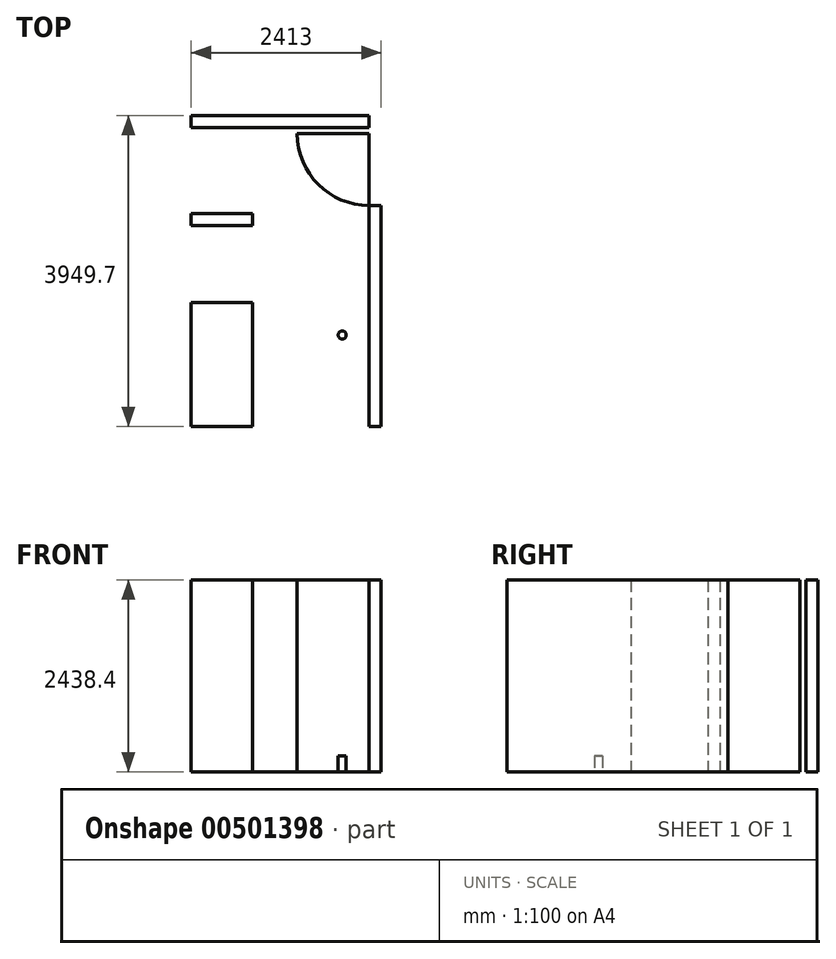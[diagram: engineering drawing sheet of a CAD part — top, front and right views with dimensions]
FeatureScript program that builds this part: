
annotation { "Feature Type Name" : "Feature", "Feature Type Description" : "" }
export const myFeature = defineFeature(function(context is Context, id is Id, definition is map)
    precondition{}
    {
        {
            var Q0;
            Q0=qCreatedBy(makeId("Top.planeOp"),FACE);
            var sketch = newSketch(context, id + "F0", { "sketchPlane" : qUnion([Q0])});
            skLineSegment(sketch, "E0.bottom", {"start": v(0, 0) * mm, "end": v(2260.6, 0) * mm});
            skLineSegment(sketch, "E0.top", {"start": v(0, 2705.1) * mm, "end": v(781.05, 2705.1) * mm});
            skLineSegment(sketch, "E0.left", {"start": v(0, 0) * mm, "end": v(0, 2705.1) * mm});
            skLineSegment(sketch, "E1", {"start": v(0, 2705.1) * mm, "end": v(0, 3797.3) * mm});
            skLineSegment(sketch, "E2", {"start": v(0, 3797.3) * mm, "end": v(2260.6, 3797.3) * mm});
            skLineSegment(sketch, "E3", {"start": v(2260.6, 3797.3) * mm, "end": v(2260.6, 0) * mm});
            skLineSegment(sketch, "E4", {"start": v(2260.6, 3797.3) * mm, "end": v(2260.6, 3721.1) * mm, "construction": true});
            skArc(sketch, "E5", {"start": v(1346.2, 3721.1) * mm, "mid": v(1614.02, 3074.52) * mm, "end": v(2260.6, 2806.7) * mm});
            skLineSegment(sketch, "E6", {"start": v(1346.2, 3721.1) * mm, "end": v(2260.6, 3721.1) * mm});
            skLineSegment(sketch, "E7", {"start": v(0, 3797.3) * mm, "end": v(0, 3721.1) * mm, "construction": true});
            skLineSegment(sketch, "E8", {"start": v(0, 3721.1) * mm, "end": v(0, 2806.7) * mm, "construction": true});
            skCircle(sketch, "E9", {"center": v(1917.7, 1162.05) * mm, "radius": 50.8 * mm});
            skLineSegment(sketch, "E10", {"start": v(781.05, 2705.1) * mm, "end": v(781.05, 2552.7) * mm});
            skLineSegment(sketch, "E11", {"start": v(781.05, 2552.7) * mm, "end": v(0, 2552.7) * mm});
            skLineSegment(sketch, "E12", {"start": v(781.05, 1574.8) * mm, "end": v(0, 1574.8) * mm});
            skLineSegment(sketch, "E13.trimOffspring", {"start": v(781.05, 1574.8) * mm, "end": v(781.05, 0) * mm});
            skLineSegment(sketch, "E14.bottom", {"start": v(2260.6, 2806.7) * mm, "end": v(2413, 2806.7) * mm});
            skLineSegment(sketch, "E14.top", {"start": v(2260.6, 0) * mm, "end": v(2413, 0) * mm});
            skLineSegment(sketch, "E14.left", {"start": v(2260.6, 2806.7) * mm, "end": v(2260.6, 0) * mm});
            skLineSegment(sketch, "E14.right", {"start": v(2413, 2806.7) * mm, "end": v(2413, 0) * mm});
            skLineSegment(sketch, "E15.top", {"start": v(0, 3949.7) * mm, "end": v(2260.6, 3949.7) * mm});
            skLineSegment(sketch, "E15.left", {"start": v(0, 3797.3) * mm, "end": v(0, 3949.7) * mm});
            skLineSegment(sketch, "E15.right", {"start": v(2260.6, 3797.3) * mm, "end": v(2260.6, 3949.7) * mm});
            skSolve(sketch);
        }
        {
            var Q0;
            Q0=makeQuery(id+"F0.imprint","IMPRINT",FACE,{"disambiguationData":[TD([[makeQuery(id+"F0.imprint","IMPRINT",EDGE,{"derivedFrom":sQuery(id+"F0.wireOp",EDGE,"E0.top")}),1.0]])]});
            var sketch = newSketch(context, id + "F1", { "sketchPlane" : qUnion([Q0])});
            skSolve(sketch);
        }
        {
            var Q0;
            {var subQ0=sQuery(id+"F0.wireOp",EDGE,"E0.top");Q0=makeQuery(id+"F0.imprint","IMPRINT",FACE,{"disambiguationData":[TD([[makeQuery(id+"F0.imprint","IMPRINT",EDGE,{"derivedFrom":subQ0}),-1.0]])]});}
            var Q1;
            {var subQ4=sQuery(id+"F0.wireOp",EDGE,"E12");Q1=makeQuery(id+"F0.imprint","IMPRINT",FACE,{"disambiguationData":[TD([[makeQuery(id+"F0.imprint","IMPRINT",EDGE,{"derivedFrom":subQ4}),1.0]])]});}
            var Q2;
            {var subQ0=sQuery(id+"F0.wireOp",EDGE,"E5");Q2=makeQuery(id+"F0.imprint","IMPRINT",FACE,{"disambiguationData":[TD([[makeQuery(id+"F0.imprint","IMPRINT",EDGE,{"derivedFrom":subQ0}),1.0]])]});}
            var Q3;
            Q3=makeQuery(id+"F0.imprint","IMPRINT",FACE,{"disambiguationData":[TD([[makeQuery(id+"F0.imprint","IMPRINT",EDGE,{"derivedFrom":sQuery(id+"F0.wireOp",EDGE,"E14.bottom")}),-1.0]])]});
            var Q4;
            Q4=makeQuery(id+"F0.imprint","IMPRINT",FACE,{"disambiguationData":[TD([[makeQuery(id+"F0.imprint","IMPRINT",EDGE,{"derivedFrom":sQuery(id+"F0.wireOp",EDGE,"E2")}),1.0]])]});
            extrude(context, id + "F2", {"entities" : qUnion([Q0, Q1, Q2, Q3, Q4]), "depth" : 2438.4 * mm});
        }
        {
            var Q0;
            Q0=makeQuery(id+"F1.imprint","IMPRINT",FACE,{"disambiguationData":[TD([[makeQuery(id+"F1.imprint","IMPRINT",EDGE,{"derivedFrom":makeQuery(id+"F0.imprint","IMPRINT",EDGE,{"derivedFrom":sQuery(id+"F0.wireOp",EDGE,"E9")})}),1.0]])]});
            extrude(context, id + "F3", {"entities" : qUnion([Q0]), "depth" : 203.2 * mm});
        }
    });
